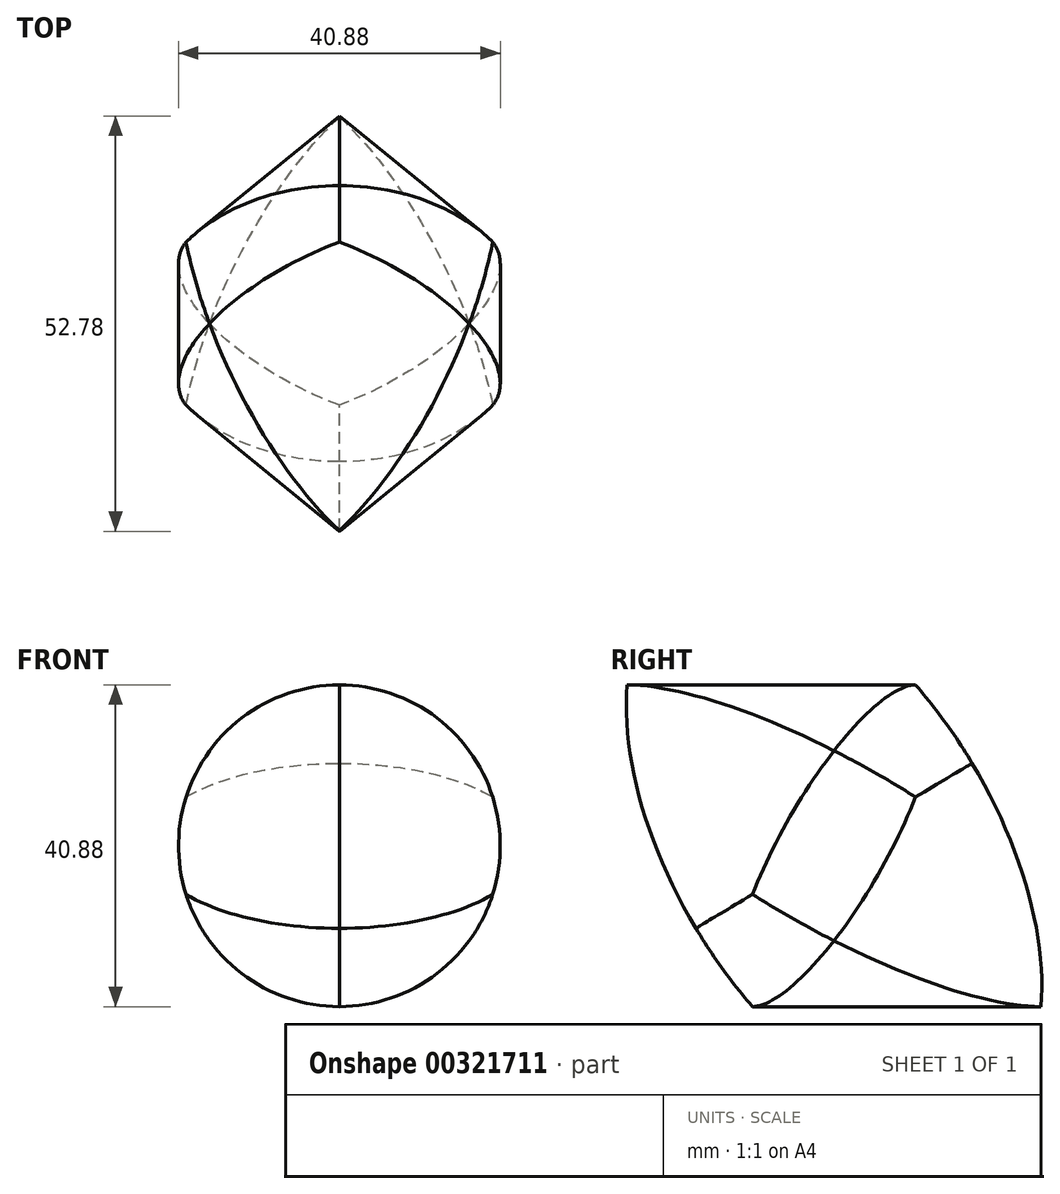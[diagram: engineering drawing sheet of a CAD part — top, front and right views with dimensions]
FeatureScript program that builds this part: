
annotation { "Feature Type Name" : "Feature", "Feature Type Description" : "" }
export const myFeature = defineFeature(function(context is Context, id is Id, definition is map)
    precondition{}
    {
        {
            var Q0;
            Q0=qCreatedBy(makeId("Front.planeOp"),FACE);
            var sketch = newSketch(context, id + "F0", { "sketchPlane" : qUnion([Q0])});
            skCircle(sketch, "E0", {"center": v(0, 0) * mm, "radius": 20.44 * mm});
            skSolve(sketch);
        }
        {
            var Q0;
            Q0=makeQuery(id+"F0.imprint","IMPRINT",FACE,{"disambiguationData":[TD([[makeQuery(id+"F0.imprint","IMPRINT",EDGE,{"derivedFrom":sQuery(id+"F0.wireOp",EDGE,"E0")}),1.0]])]});
            extrude(context, id + "F1", {"entities" : qUnion([Q0]), "endBound" : BoundingType.SYMMETRIC, "depth" : 80 * mm});
        }
        {
            var Q0;
            Q0=qCreatedBy(makeId("Front.planeOp"),FACE);
            var Q1;
            Q1=qCreatedBy(makeId("Right.planeOp"),FACE);
            cPlane(context, id + "F2", {"entities" : qUnion([Q0, Q1]), "cplaneType" : CPlaneType.MID_PLANE, "offset" : 25 * mm, "width" : 150 * mm, "height" : 150 * mm});
        }
        {
            var Q0;
            Q0=qCreatedBy(makeId("Right.planeOp"),FACE);
            var sketch = newSketch(context, id + "F3", { "sketchPlane" : qUnion([Q0])});
            skLineSegment(sketch, "E1", {"start": v(0, 0) * mm, "end": v(-28.28, 22) * mm});
            skSolve(sketch);
        }
        {
            var Q0;
            Q0=makeQuery(id+"F1.opExtrude","SWEPT_BODY",BODY,{"disambiguationData":[OSD([sQuery(id+"F0.wireOp",EDGE,"E0")])]});
            var Q1;
            Q1=sQuery(id+"F3.wireOp",EDGE,"E1");
            circularPattern(context, id + "F4", {"entities" : qUnion([Q0]), "axis" : qUnion([Q1]), "angle" : 360 * degree, "instanceCount" : 3, "equalSpace" : true});
        }
        {
            var Q0;
            Q0=makeQuery(id+"F4.opPattern","COPY",BODY,{"derivedFrom":makeQuery(id+"F1.opExtrude","SWEPT_BODY",BODY,{"disambiguationData":[OSD([sQuery(id+"F0.wireOp",EDGE,"E0")])]}),"instanceName":"2"});
            var Q1;
            Q1=makeQuery(id+"F4.opPattern","COPY",BODY,{"derivedFrom":makeQuery(id+"F1.opExtrude","SWEPT_BODY",BODY,{"disambiguationData":[OSD([sQuery(id+"F0.wireOp",EDGE,"E0")])]}),"instanceName":"1"});
            var Q2;
            Q2=makeQuery(id+"F1.opExtrude","SWEPT_BODY",BODY,{"disambiguationData":[OSD([sQuery(id+"F0.wireOp",EDGE,"E0")])]});
            booleanBodies(context, id + "F5", {"operationType" : BooleanOperationType.INTERSECTION, "tools" : qUnion([Q0, Q1, Q2])});
        }
    });
